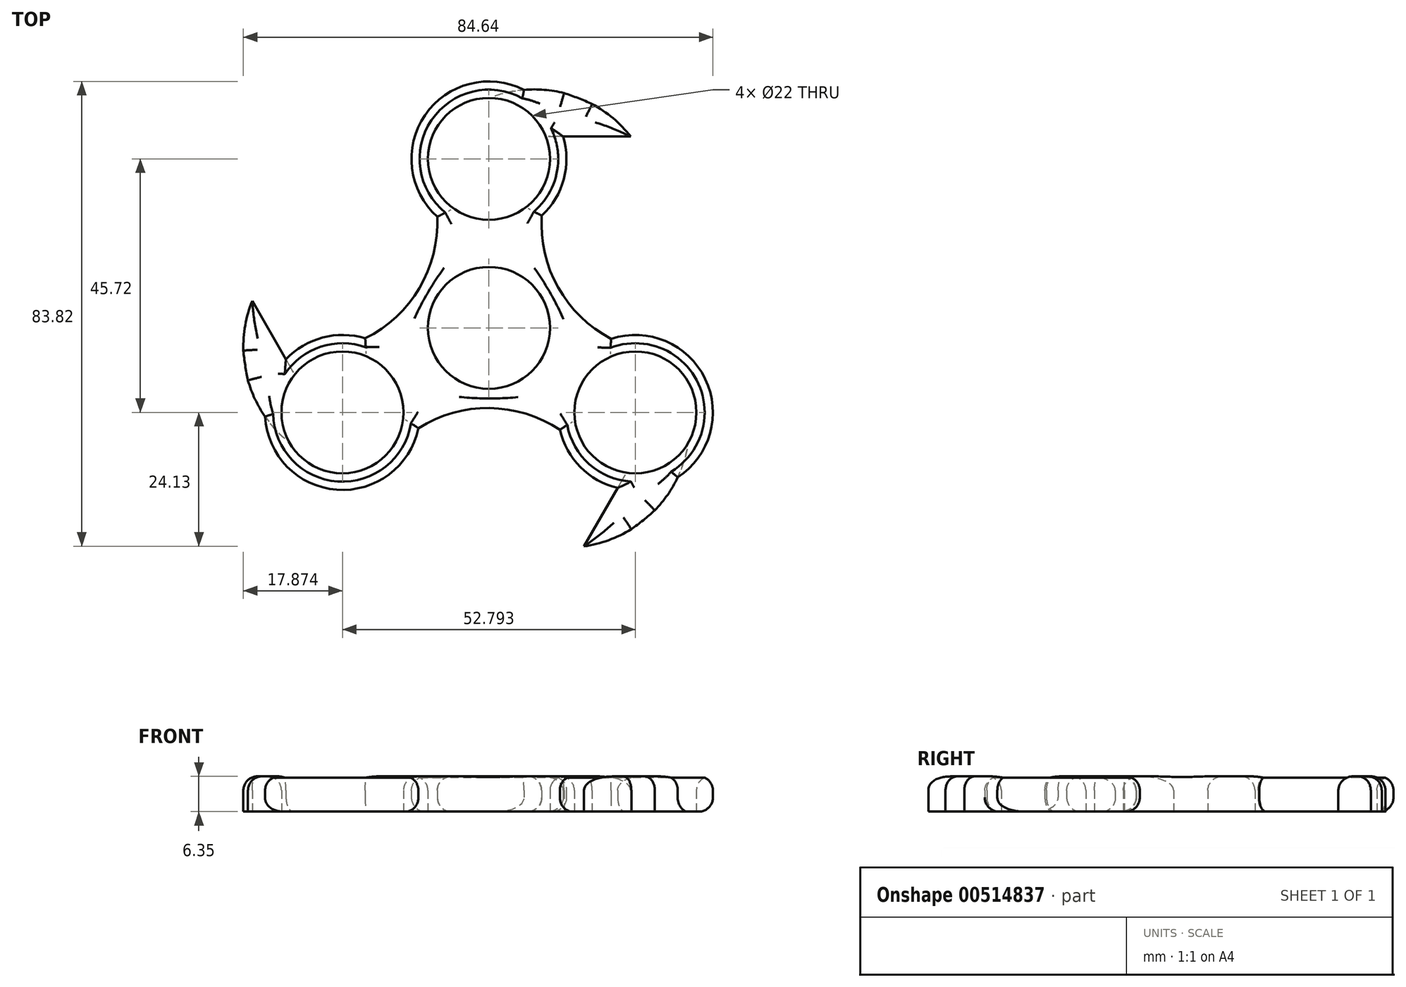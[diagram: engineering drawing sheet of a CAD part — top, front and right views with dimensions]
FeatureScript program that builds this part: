
annotation { "Feature Type Name" : "Feature", "Feature Type Description" : "" }
export const myFeature = defineFeature(function(context is Context, id is Id, definition is map)
    precondition{}
    {
        {
            var Q0;
            Q0=qCreatedBy(makeId("Top.planeOp"),FACE);
            var sketch = newSketch(context, id + "F0", { "sketchPlane" : qUnion([Q0])});
            skCircle(sketch, "E0", {"center": v(0, 0) * mm, "radius": 44.45 * mm});
            skCircle(sketch, "E1", {"center": v(0, 0) * mm, "radius": 11 * mm});
            skLineSegment(sketch, "E2", {"start": v(0, 0) * mm, "end": v(0, 30.48) * mm});
            skCircle(sketch, "E3", {"center": v(0, 30.48) * mm, "radius": 11 * mm});
            skCircle(sketch, "E4", {"center": v(0, 30.48) * mm, "radius": 13.97 * mm});
            skCircle(sketch, "E5.1.0", {"center": v(-26.4, -15.24) * mm, "radius": 11 * mm});
            skCircle(sketch, "E5.1.1", {"center": v(-26.4, -15.24) * mm, "radius": 13.97 * mm});
            skCircle(sketch, "E5.2.0", {"center": v(26.4, -15.24) * mm, "radius": 11 * mm});
            skCircle(sketch, "E5.2.1", {"center": v(26.4, -15.24) * mm, "radius": 13.97 * mm});
            skCircle(sketch, "E6", {"center": v(0, 0) * mm, "radius": 13.97 * mm});
            skArc(sketch, "E7", {"start": v(12.78, -18.38) * mm, "mid": v(0.07, -14.45) * mm, "end": v(-12.72, -18.09) * mm});
            skArc(sketch, "E8.1.0", {"start": v(9.52, 20.26) * mm, "mid": v(12.48, 7.29) * mm, "end": v(22.02, -1.97) * mm});
            skArc(sketch, "E8.2.0", {"start": v(-22.3, -1.88) * mm, "mid": v(-12.55, 7.16) * mm, "end": v(-9.3, 20.06) * mm});
            skLineSegment(sketch, "E9", {"start": v(13.37, 34.52) * mm, "end": v(25.54, 34.52) * mm});
            skArc(sketch, "E10", {"start": v(25.54, 34.52) * mm, "mid": v(17, 41.15) * mm, "end": v(6.33, 42.94) * mm});
            skArc(sketch, "E11.1.0", {"start": v(-42.66, 4.85) * mm, "mid": v(-44.14, -5.86) * mm, "end": v(-40.35, -15.99) * mm});
            skLineSegment(sketch, "E11.1.1", {"start": v(-36.58, -5.68) * mm, "end": v(-42.66, 4.85) * mm});
            skArc(sketch, "E11.2.0", {"start": v(17.13, -39.37) * mm, "mid": v(27.14, -35.3) * mm, "end": v(34.02, -26.95) * mm});
            skLineSegment(sketch, "E11.2.1", {"start": v(23.2, -28.84) * mm, "end": v(17.13, -39.37) * mm});
            skSolve(sketch);
        }
        {
            var Q0;
            Q0=makeQuery(id+"F0.imprint","IMPRINT",FACE,{"disambiguationData":[TD([[makeQuery(id+"F0.imprint","IMPRINT",EDGE,{"derivedFrom":sQuery(id+"F0.wireOp",EDGE,"E6")}),-1.0]])]});
            var Q1;
            Q1=makeQuery(id+"F0.imprint","IMPRINT",FACE,{"disambiguationData":[TD([[makeQuery(id+"F0.imprint","IMPRINT",EDGE,{"derivedFrom":sQuery(id+"F0.wireOp",EDGE,"E3")}),-1.0]])]});
            var Q2;
            Q2=makeQuery(id+"F0.imprint","IMPRINT",FACE,{"disambiguationData":[TD([[makeQuery(id+"F0.imprint","IMPRINT",EDGE,{"derivedFrom":sQuery(id+"F0.wireOp",EDGE,"E5.2.0")}),-1.0]])]});
            var Q3;
            Q3=makeQuery(id+"F0.imprint","IMPRINT",FACE,{"disambiguationData":[TD([[makeQuery(id+"F0.imprint","IMPRINT",EDGE,{"derivedFrom":sQuery(id+"F0.wireOp",EDGE,"E5.1.0")}),-1.0]])]});
            var Q4;
            Q4=makeQuery(id+"F0.imprint","IMPRINT",FACE,{"disambiguationData":[TD([[makeQuery(id+"F0.imprint","IMPRINT",EDGE,{"derivedFrom":sQuery(id+"F0.wireOp",EDGE,"E1")}),-1.0]])]});
            var Q5;
            {var subQ1=sQuery(id+"F0.wireOp",EDGE,"E9");Q5=makeQuery(id+"F0.imprint","IMPRINT",FACE,{"disambiguationData":[TD([[makeQuery(id+"F0.imprint","IMPRINT",EDGE,{"derivedFrom":subQ1}),1.0]])]});}
            var Q6;
            {var subQ5=sQuery(id+"F0.wireOp",EDGE,"E11.2.1");Q6=makeQuery(id+"F0.imprint","IMPRINT",FACE,{"disambiguationData":[TD([[makeQuery(id+"F0.imprint","IMPRINT",EDGE,{"derivedFrom":subQ5}),1.0]])]});}
            var Q7;
            {var subQ5=sQuery(id+"F0.wireOp",EDGE,"E11.1.1");Q7=makeQuery(id+"F0.imprint","IMPRINT",FACE,{"disambiguationData":[TD([[makeQuery(id+"F0.imprint","IMPRINT",EDGE,{"derivedFrom":subQ5}),1.0]])]});}
            extrude(context, id + "F1", {"entities" : qUnion([Q0, Q1, Q2, Q3, Q4, Q5, Q6, Q7]), "depth" : 6.35 * mm, "offsetDistance" : 25.4 * mm});
        }
        {
            var Q0;
            Q0=makeQuery(id+"F1.opExtrude","CAP_EDGE",EDGE,{"disambiguationData":[OSD([sQuery(id+"F0.wireOp",EDGE,"E8.2.0")])],"isStart":false});
            var Q1;
            Q1=makeQuery(id+"F1.opExtrude","CAP_EDGE",EDGE,{"disambiguationData":[OSD([sQuery(id+"F0.wireOp",EDGE,"E8.1.0")])],"isStart":false});
            var Q2;
            Q2=makeQuery(id+"F1.opExtrude","CAP_EDGE",EDGE,{"disambiguationData":[OSD([sQuery(id+"F0.wireOp",EDGE,"E7")])],"isStart":false});
            var Q3;
            Q3=makeQuery(id+"F1.opExtrude","CAP_EDGE",EDGE,{"disambiguationData":[OSD([sQuery(id+"F0.wireOp",EDGE,"E5.1.1")])],"isStart":false});
            var Q4;
            Q4=makeQuery(id+"F1.opExtrude","CAP_EDGE",EDGE,{"disambiguationData":[OSD([sQuery(id+"F0.wireOp",EDGE,"E5.2.1")])],"isStart":false});
            var Q5;
            Q5=makeQuery(id+"F1.opExtrude","CAP_EDGE",EDGE,{"disambiguationData":[OSD([sQuery(id+"F0.wireOp",EDGE,"E4")])],"isStart":false});
            var Q6;
            Q6=makeQuery(id+"F1.opExtrude","CAP_EDGE",EDGE,{"disambiguationData":[OSD([sQuery(id+"F0.wireOp",EDGE,"E8.2.0")])],"isStart":true});
            var Q7;
            Q7=makeQuery(id+"F1.opExtrude","CAP_EDGE",EDGE,{"disambiguationData":[OSD([sQuery(id+"F0.wireOp",EDGE,"E5.1.1")])],"isStart":true});
            var Q8;
            Q8=makeQuery(id+"F1.opExtrude","CAP_EDGE",EDGE,{"disambiguationData":[OSD([sQuery(id+"F0.wireOp",EDGE,"E7")])],"isStart":true});
            var Q9;
            Q9=makeQuery(id+"F1.opExtrude","CAP_EDGE",EDGE,{"disambiguationData":[OSD([sQuery(id+"F0.wireOp",EDGE,"E5.2.1")])],"isStart":true});
            var Q10;
            Q10=makeQuery(id+"F1.opExtrude","CAP_EDGE",EDGE,{"disambiguationData":[OSD([sQuery(id+"F0.wireOp",EDGE,"E8.1.0")])],"isStart":true});
            var Q11;
            Q11=makeQuery(id+"F1.opExtrude","CAP_EDGE",EDGE,{"disambiguationData":[OSD([sQuery(id+"F0.wireOp",EDGE,"E4")])],"isStart":true});
            var Q12;
            {var subQ0=sQuery(id+"F0.wireOp",EDGE,"E11.1.0");var subQ1=sQuery(id+"F0.wireOp",EDGE,"E0");Q12=makeQuery(id+"F1.opExtrude","CAP_EDGE",EDGE,{"disambiguationData":[OSD([subQ1]),TDD([makeQuery(id+"F0.imprint","IMPRINT",EDGE,{"disambiguationData":[TD([[makeQuery(id+"F0.imprint","INTERSECT",VERTEX,{"disambiguationData":[OD(0.0)],"derivedFrom":[subQ1,subQ0]}),-1.0]])],"derivedFrom":subQ1})])],"isStart":false});}
            var Q13;
            {var subQ0=sQuery(id+"F0.wireOp",EDGE,"E11.1.0");Q13=makeQuery(id+"F1.opExtrude","CAP_EDGE",EDGE,{"disambiguationData":[OSD([subQ0]),TDD([makeQuery(id+"F0.imprint","IMPRINT",EDGE,{"disambiguationData":[TD([[makeQuery(id+"F0.imprint","INTERSECT",VERTEX,{"derivedFrom":[subQ0,sQuery(id+"F0.wireOp",EDGE,"E11.1.1")]}),-1.0]])],"derivedFrom":subQ0})])],"isStart":false});}
            var Q14;
            {var subQ0=sQuery(id+"F0.wireOp",EDGE,"E11.1.0");Q14=makeQuery(id+"F1.opExtrude","CAP_EDGE",EDGE,{"disambiguationData":[OSD([subQ0]),TDD([makeQuery(id+"F0.imprint","IMPRINT",EDGE,{"disambiguationData":[TD([[makeQuery(id+"F0.imprint","INTERSECT",VERTEX,{"derivedFrom":[sQuery(id+"F0.wireOp",EDGE,"E5.1.1"),subQ0]}),1.0]])],"derivedFrom":subQ0})])],"isStart":false});}
            var Q15;
            Q15=makeQuery(id+"F1.opExtrude","CAP_EDGE",EDGE,{"disambiguationData":[OSD([sQuery(id+"F0.wireOp",EDGE,"E11.1.1")])],"isStart":false});
            var Q16;
            {var subQ0=sQuery(id+"F0.wireOp",EDGE,"E11.2.0");Q16=makeQuery(id+"F1.opExtrude","CAP_EDGE",EDGE,{"disambiguationData":[OSD([subQ0]),TDD([makeQuery(id+"F0.imprint","IMPRINT",EDGE,{"disambiguationData":[TD([[makeQuery(id+"F0.imprint","INTERSECT",VERTEX,{"derivedFrom":[sQuery(id+"F0.wireOp",EDGE,"E5.2.1"),subQ0]}),1.0]])],"derivedFrom":subQ0})])],"isStart":false});}
            var Q17;
            {var subQ0=sQuery(id+"F0.wireOp",EDGE,"E11.2.0");var subQ1=sQuery(id+"F0.wireOp",EDGE,"E0");Q17=makeQuery(id+"F1.opExtrude","CAP_EDGE",EDGE,{"disambiguationData":[OSD([subQ1]),TDD([makeQuery(id+"F0.imprint","IMPRINT",EDGE,{"disambiguationData":[TD([[makeQuery(id+"F0.imprint","INTERSECT",VERTEX,{"disambiguationData":[OD(0.0)],"derivedFrom":[subQ1,subQ0]}),-1.0]])],"derivedFrom":subQ1})])],"isStart":false});}
            var Q18;
            {var subQ0=sQuery(id+"F0.wireOp",EDGE,"E11.2.0");Q18=makeQuery(id+"F1.opExtrude","CAP_EDGE",EDGE,{"disambiguationData":[OSD([subQ0]),TDD([makeQuery(id+"F0.imprint","IMPRINT",EDGE,{"disambiguationData":[TD([[makeQuery(id+"F0.imprint","INTERSECT",VERTEX,{"derivedFrom":[subQ0,sQuery(id+"F0.wireOp",EDGE,"E11.2.1")]}),-1.0]])],"derivedFrom":subQ0})])],"isStart":false});}
            var Q19;
            Q19=makeQuery(id+"F1.opExtrude","CAP_EDGE",EDGE,{"disambiguationData":[OSD([sQuery(id+"F0.wireOp",EDGE,"E11.2.1")])],"isStart":false});
            var Q20;
            {var subQ0=sQuery(id+"F0.wireOp",EDGE,"E10");var subQ1=sQuery(id+"F0.wireOp",EDGE,"E0");Q20=makeQuery(id+"F1.opExtrude","CAP_EDGE",EDGE,{"disambiguationData":[OSD([subQ1]),TDD([makeQuery(id+"F0.imprint","IMPRINT",EDGE,{"disambiguationData":[TD([[makeQuery(id+"F0.imprint","INTERSECT",VERTEX,{"disambiguationData":[OD(0.0)],"derivedFrom":[subQ1,subQ0]}),1.0]])],"derivedFrom":subQ1})])],"isStart":false});}
            var Q21;
            {var subQ0=sQuery(id+"F0.wireOp",EDGE,"E10");Q21=makeQuery(id+"F1.opExtrude","CAP_EDGE",EDGE,{"disambiguationData":[OSD([subQ0]),TDD([makeQuery(id+"F0.imprint","IMPRINT",EDGE,{"disambiguationData":[TD([[makeQuery(id+"F0.imprint","INTERSECT",VERTEX,{"derivedFrom":[sQuery(id+"F0.wireOp",EDGE,"E4"),subQ0]}),1.0]])],"derivedFrom":subQ0})])],"isStart":false});}
            var Q22;
            {var subQ0=sQuery(id+"F0.wireOp",EDGE,"E10");Q22=makeQuery(id+"F1.opExtrude","CAP_EDGE",EDGE,{"disambiguationData":[OSD([subQ0]),TDD([makeQuery(id+"F0.imprint","IMPRINT",EDGE,{"disambiguationData":[TD([[makeQuery(id+"F0.imprint","INTERSECT",VERTEX,{"derivedFrom":[sQuery(id+"F0.wireOp",EDGE,"E9"),subQ0]}),-1.0]])],"derivedFrom":subQ0})])],"isStart":false});}
            var Q23;
            Q23=makeQuery(id+"F1.opExtrude","CAP_FACE",FACE,{"disambiguationData":[OSD([sQuery(id+"F0.wireOp",EDGE,"E0"),sQuery(id+"F0.wireOp",EDGE,"E1"),sQuery(id+"F0.wireOp",EDGE,"E3"),sQuery(id+"F0.wireOp",EDGE,"E4"),sQuery(id+"F0.wireOp",EDGE,"E5.1.0"),sQuery(id+"F0.wireOp",EDGE,"E5.1.1"),sQuery(id+"F0.wireOp",EDGE,"E5.2.0"),sQuery(id+"F0.wireOp",EDGE,"E5.2.1"),sQuery(id+"F0.wireOp",EDGE,"E7"),sQuery(id+"F0.wireOp",EDGE,"E8.1.0"),sQuery(id+"F0.wireOp",EDGE,"E8.2.0"),sQuery(id+"F0.wireOp",EDGE,"E9"),sQuery(id+"F0.wireOp",EDGE,"E10"),sQuery(id+"F0.wireOp",EDGE,"E11.1.0"),sQuery(id+"F0.wireOp",EDGE,"E11.1.1"),sQuery(id+"F0.wireOp",EDGE,"E11.2.0"),sQuery(id+"F0.wireOp",EDGE,"E11.2.1")])],"isStart":false});
            fillet(context, id + "F2", {"entities" : qUnion([Q0, Q1, Q2, Q3, Q4, Q5, Q6, Q7, Q8, Q9, Q10, Q11, Q12, Q13, Q14, Q15, Q16, Q17, Q18, Q19, Q20, Q21, Q22, Q23]), "radius" : 2.54 * mm, "tangentPropagation" : true, "allowEdgeOverflow" : false});
        }
    });
